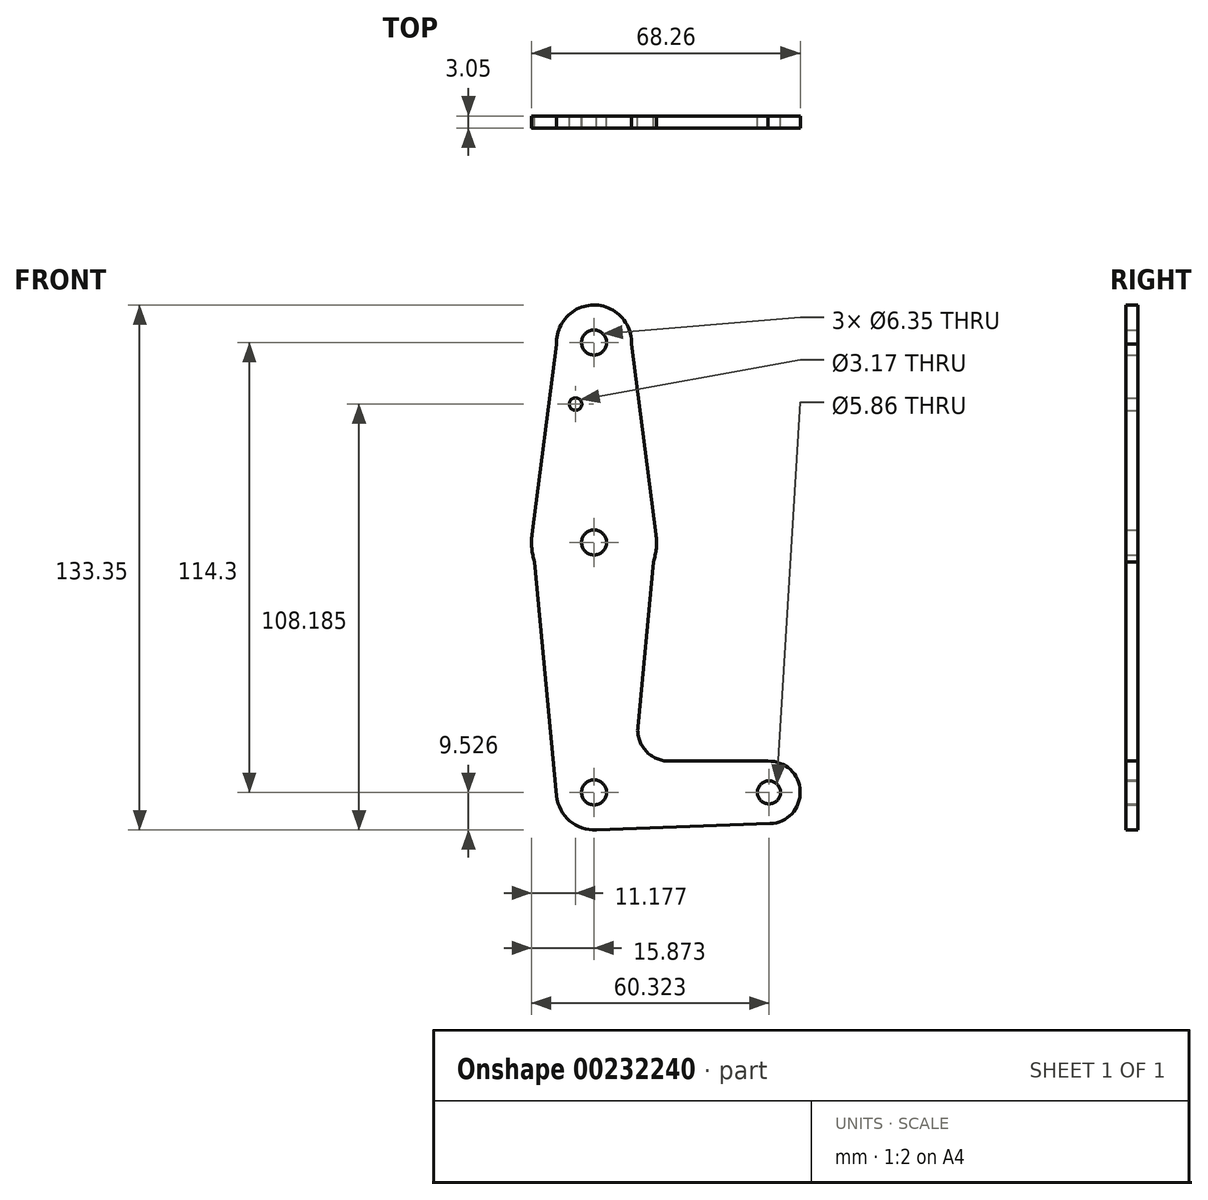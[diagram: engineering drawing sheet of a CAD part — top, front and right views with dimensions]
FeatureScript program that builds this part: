
annotation { "Feature Type Name" : "Feature", "Feature Type Description" : "" }
export const myFeature = defineFeature(function(context is Context, id is Id, definition is map)
    precondition{}
    {
        {
            var Q0;
            Q0=qCreatedBy(makeId("Front.planeOp"),FACE);
            var sketch = newSketch(context, id + "F0", { "sketchPlane" : qUnion([Q0])});
            skLineSegment(sketch, "E0", {"start": v(-46.85, 70.54) * mm, "end": v(-46.85, -43.76) * mm, "construction": true});
            skLineSegment(sketch, "E1", {"start": v(-46.85, -43.76) * mm, "end": v(-2.4, -43.76) * mm, "construction": true});
            skCircle(sketch, "E2", {"center": v(-46.85, 70.54) * mm, "radius": 9.53 * mm});
            skCircle(sketch, "E3", {"center": v(-46.85, 19.74) * mm, "radius": 15.88 * mm});
            skCircle(sketch, "E4", {"center": v(-46.85, -43.76) * mm, "radius": 9.53 * mm});
            skCircle(sketch, "E5", {"center": v(-2.4, -43.76) * mm, "radius": 7.94 * mm});
            skLineSegment(sketch, "E6", {"start": v(-56.36, 70) * mm, "end": v(-62.6, 21.77) * mm});
            skLineSegment(sketch, "E7", {"start": v(-62.6, 21.77) * mm, "end": v(-56.33, -44.66) * mm});
            skLineSegment(sketch, "E8", {"start": v(-37.33, 70.17) * mm, "end": v(-31.1, 21.76) * mm});
            skLineSegment(sketch, "E9", {"start": v(-31.1, 21.76) * mm, "end": v(-35.71, -27.13) * mm});
            skLineSegment(sketch, "E10", {"start": v(-46.8, -53.29) * mm, "end": v(-2.11, -51.7) * mm});
            skLineSegment(sketch, "E11", {"start": v(-2.66, -35.83) * mm, "end": v(-27.8, -35.83) * mm});
            skCircle(sketch, "E12", {"center": v(-51.54, 54.9) * mm, "radius": 1.59 * mm});
            skCircle(sketch, "E13", {"center": v(-46.85, 70.54) * mm, "radius": 3.18 * mm});
            skCircle(sketch, "E14", {"center": v(-46.85, 19.74) * mm, "radius": 3.18 * mm});
            skCircle(sketch, "E15", {"center": v(-46.85, -43.76) * mm, "radius": 3.18 * mm});
            skCircle(sketch, "E16", {"center": v(-2.4, -43.76) * mm, "radius": 2.93 * mm});
            skArc(sketch, "E17.filletArc", {"start": v(-35.71, -27.13) * mm, "mid": v(-33.68, -33.23) * mm, "end": v(-27.8, -35.83) * mm});
            skSolve(sketch);
        }
        {
            var Q0;
            Q0 = qSketchRegion(id + "F0", true);
            extrude(context, id + "F1", {"entities" : qUnion([Q0]), "depth" : 3.05 * mm});
        }
    });
